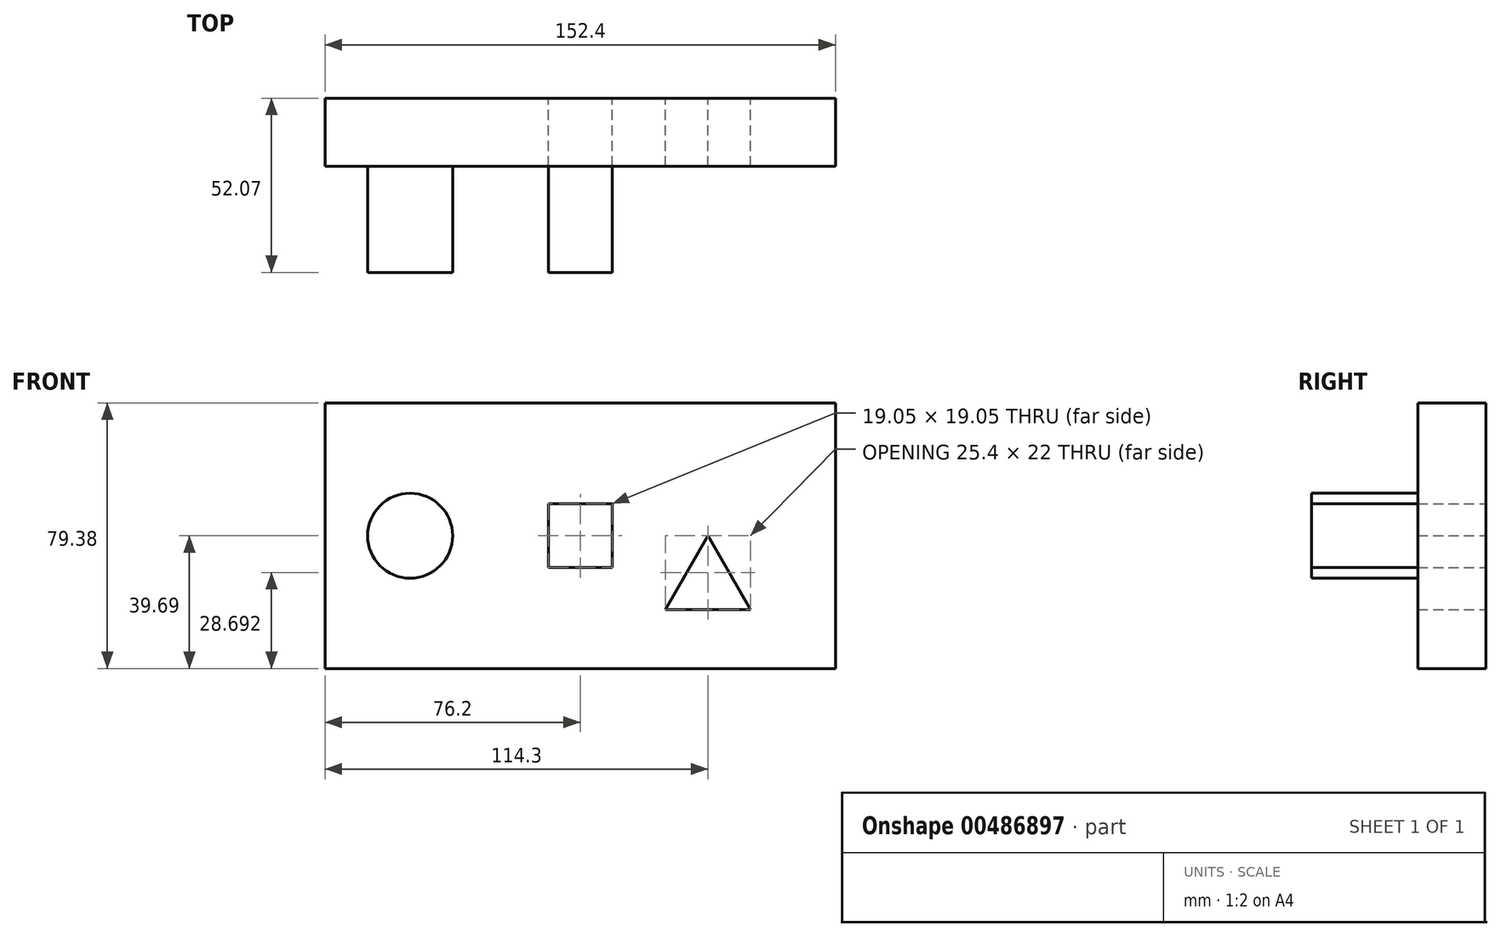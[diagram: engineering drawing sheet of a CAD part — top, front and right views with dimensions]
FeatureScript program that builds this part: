
annotation { "Feature Type Name" : "Feature", "Feature Type Description" : "" }
export const myFeature = defineFeature(function(context is Context, id is Id, definition is map)
    precondition{}
    {
        {
            var Q0;
            Q0=qCreatedBy(makeId("Front.planeOp"),FACE);
            var sketch = newSketch(context, id + "F0", { "sketchPlane" : qUnion([Q0])});
            skLineSegment(sketch, "E0", {"start": v(0, -39.67) * mm, "end": v(44.45, -39.67) * mm});
            skLineSegment(sketch, "E1", {"start": v(44.45, -39.67) * mm, "end": v(44.45, 0) * mm});
            skLineSegment(sketch, "E2", {"start": v(44.45, 0) * mm, "end": v(44.45, 39.69) * mm});
            skLineSegment(sketch, "E3.bottom", {"start": v(44.45, 39.69) * mm, "end": v(-107.95, 39.69) * mm});
            skLineSegment(sketch, "E3.top", {"start": v(44.45, -39.69) * mm, "end": v(-107.95, -39.69) * mm});
            skLineSegment(sketch, "E3.left", {"start": v(44.45, 39.69) * mm, "end": v(44.45, -39.69) * mm});
            skLineSegment(sketch, "E3.right", {"start": v(-107.95, 39.69) * mm, "end": v(-107.95, -39.69) * mm});
            skLineSegment(sketch, "E4", {"start": v(0, 0) * mm, "end": v(6.35, 0) * mm});
            skLineSegment(sketch, "E5", {"start": v(0, 0) * mm, "end": v(-31.75, 0) * mm});
            skLineSegment(sketch, "E6.bottom", {"start": v(-41.27, 9.52) * mm, "end": v(-22.23, 9.52) * mm});
            skLineSegment(sketch, "E6.top", {"start": v(-41.27, -9.53) * mm, "end": v(-22.23, -9.53) * mm});
            skLineSegment(sketch, "E6.left", {"start": v(-41.27, 9.52) * mm, "end": v(-41.27, -9.53) * mm});
            skLineSegment(sketch, "E6.right", {"start": v(-22.23, 9.52) * mm, "end": v(-22.23, -9.53) * mm});
            skPoint(sketch, "E6.middle", {"position": v(-31.75, 0) * mm});
            skLineSegment(sketch, "E7", {"start": v(-31.75, 0) * mm, "end": v(-82.55, 0) * mm});
            skCircle(sketch, "E8", {"center": v(-82.55, 0) * mm, "radius": 12.7 * mm});
            skLineSegment(sketch, "E9", {"start": v(6.35, 0) * mm, "end": v(6.35, -22) * mm});
            skLineSegment(sketch, "E10", {"start": v(6.35, -22) * mm, "end": v(19.05, -22) * mm});
            skLineSegment(sketch, "E11", {"start": v(6.35, 0) * mm, "end": v(19.05, -22) * mm});
            skLineSegment(sketch, "E12", {"start": v(6.35, -22) * mm, "end": v(-6.35, -22) * mm});
            skLineSegment(sketch, "E13", {"start": v(-6.35, -22) * mm, "end": v(6.35, 0) * mm});
            skSolve(sketch);
        }
        {
            var Q0;
            {var subQ6=sQuery(id+"F0.wireOp",EDGE,"E3.bottom");Q0=makeQuery(id+"F0.imprint","IMPRINT",FACE,{"disambiguationData":[TD([[makeQuery(id+"F0.imprint","IMPRINT",EDGE,{"derivedFrom":subQ6}),1.0]])]});}
            extrude(context, id + "F1", {"entities" : qUnion([Q0]), "depth" : 20.32 * mm});
        }
        {
            var Q0;
            Q0=makeQuery(id+"F0.imprint","IMPRINT",FACE,{"disambiguationData":[TD([[makeQuery(id+"F0.imprint","IMPRINT",EDGE,{"derivedFrom":sQuery(id+"F0.wireOp",EDGE,"E9")}),1.0]])]});
            var Q1;
            Q1=makeQuery(id+"F0.imprint","IMPRINT",FACE,{"disambiguationData":[TD([[makeQuery(id+"F0.imprint","IMPRINT",EDGE,{"derivedFrom":sQuery(id+"F0.wireOp",EDGE,"E9")}),-1.0]])]});
            extrude(context, id + "F2", {"entities" : qUnion([Q0, Q1]), "operationType" : NewBodyOperationType.REMOVE, "depth" : 20.32 * mm});
        }
        {
            var Q0;
            Q0=makeQuery(id+"F0.imprint","IMPRINT",FACE,{"disambiguationData":[TD([[makeQuery(id+"F0.imprint","IMPRINT",EDGE,{"derivedFrom":sQuery(id+"F0.wireOp",EDGE,"E8")}),1.0]])]});
            extrude(context, id + "F3", {"entities" : qUnion([Q0]), "operationType" : NewBodyOperationType.ADD, "depth" : 52.07 * mm});
        }
        {
            var Q0;
            {var subQ1=sQuery(id+"F0.wireOp",EDGE,"E6.bottom");Q0=makeQuery(id+"F0.imprint","IMPRINT",FACE,{"disambiguationData":[TD([[makeQuery(id+"F0.imprint","IMPRINT",EDGE,{"derivedFrom":subQ1}),-1.0]])]});}
            var Q1;
            {var subQ1=sQuery(id+"F0.wireOp",EDGE,"E6.top");Q1=makeQuery(id+"F0.imprint","IMPRINT",FACE,{"disambiguationData":[TD([[makeQuery(id+"F0.imprint","IMPRINT",EDGE,{"derivedFrom":subQ1}),1.0]])]});}
            extrude(context, id + "F4", {"entities" : qUnion([Q0, Q1]), "operationType" : NewBodyOperationType.ADD, "depth" : 52.07 * mm});
        }
        {
            var Q0;
            Q0=qCreatedBy(makeId("Front.planeOp"),FACE);
            var sketch = newSketch(context, id + "F5", { "sketchPlane" : qUnion([Q0])});
            skLineSegment(sketch, "E14", {"start": v(0, 0) * mm, "end": v(-31.75, 0) * mm});
            skLineSegment(sketch, "E15.bottom", {"start": v(-41.27, 9.52) * mm, "end": v(-22.22, 9.52) * mm});
            skLineSegment(sketch, "E15.top", {"start": v(-41.27, -9.53) * mm, "end": v(-22.22, -9.53) * mm});
            skLineSegment(sketch, "E15.left", {"start": v(-41.27, 9.52) * mm, "end": v(-41.27, -9.53) * mm});
            skLineSegment(sketch, "E15.right", {"start": v(-22.22, 9.52) * mm, "end": v(-22.22, -9.53) * mm});
            skPoint(sketch, "E15.middle", {"position": v(-31.75, 0) * mm});
            skSolve(sketch);
        }
        {
            var Q0;
            {var subQ0=sQuery(id+"F5.wireOp",EDGE,"E15.bottom");Q0=makeQuery(id+"F5.imprint","IMPRINT",FACE,{"disambiguationData":[TD([[makeQuery(id+"F5.imprint","IMPRINT",EDGE,{"derivedFrom":subQ0}),-1.0]])]});}
            extrude(context, id + "F6", {"entities" : qUnion([Q0]), "operationType" : NewBodyOperationType.REMOVE, "endBound" : BoundingType.SYMMETRIC, "depth" : 40.64 * mm});
        }
    });
